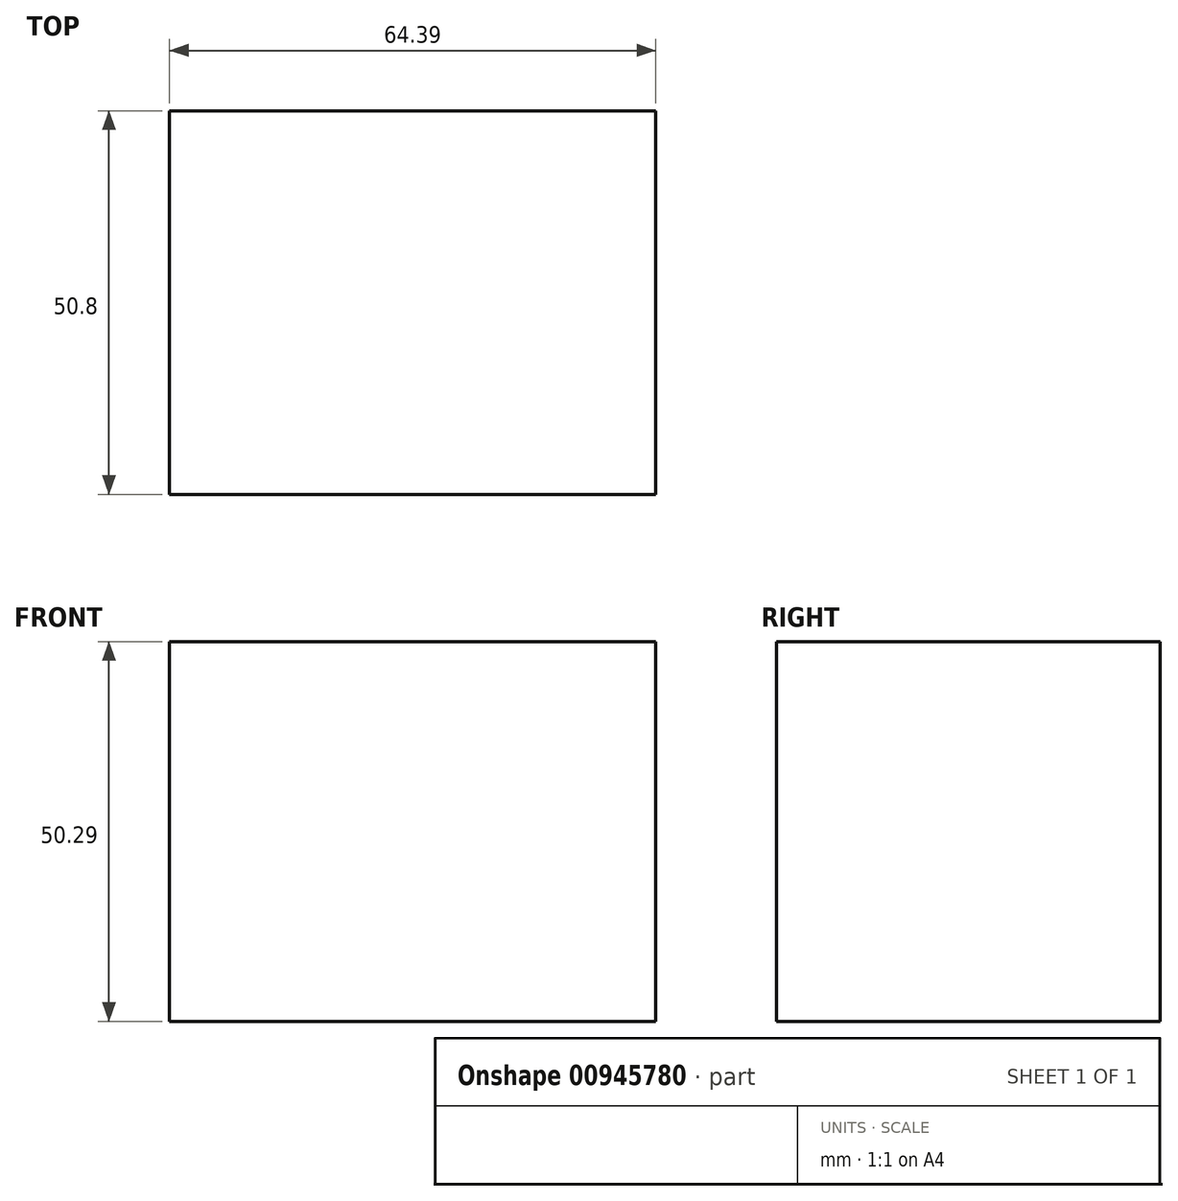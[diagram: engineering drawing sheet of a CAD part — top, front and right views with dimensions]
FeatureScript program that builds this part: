
annotation { "Feature Type Name" : "Feature", "Feature Type Description" : "" }
export const myFeature = defineFeature(function(context is Context, id is Id, definition is map)
    precondition{}
    {
        {
            var Q0;
            Q0=qCreatedBy(makeId("Top.planeOp"),FACE);
            var sketch = newSketch(context, id + "F0", { "sketchPlane" : qUnion([Q0])});
            skLineSegment(sketch, "E0.bottom", {"start": v(-43.7, 19.74) * mm, "end": v(20.7, 19.74) * mm});
            skLineSegment(sketch, "E0.top", {"start": v(-43.7, -31.06) * mm, "end": v(20.7, -31.06) * mm});
            skLineSegment(sketch, "E0.left", {"start": v(-43.7, 19.74) * mm, "end": v(-43.7, -31.06) * mm});
            skLineSegment(sketch, "E0.right", {"start": v(20.7, 19.74) * mm, "end": v(20.7, -31.06) * mm});
            skSolve(sketch);
        }
        {
            var Q0;
            Q0=makeQuery(id+"F0.imprint","IMPRINT",FACE,{"disambiguationData":[TD([[makeQuery(id+"F0.imprint","IMPRINT",EDGE,{"derivedFrom":sQuery(id+"F0.wireOp",EDGE,"E0.bottom")}),-1.0]])]});
            extrude(context, id + "F1", {"entities" : qUnion([Q0]), "depth" : 50.3 * mm, "offsetDistance" : 25.4 * mm});
        }
    });
